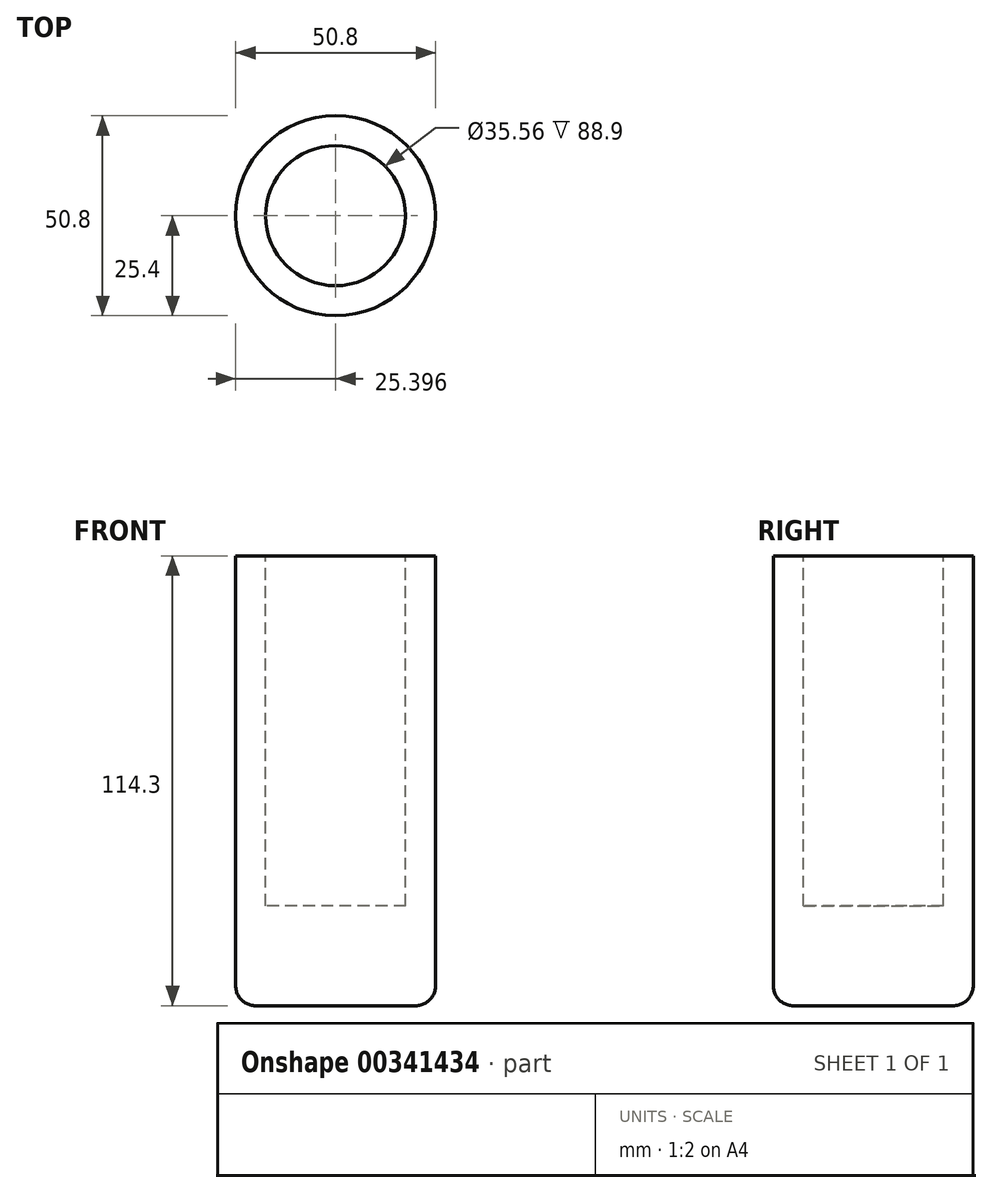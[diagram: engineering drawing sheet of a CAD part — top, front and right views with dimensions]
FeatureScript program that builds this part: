
annotation { "Feature Type Name" : "Feature", "Feature Type Description" : "" }
export const myFeature = defineFeature(function(context is Context, id is Id, definition is map)
    precondition{}
    {
        {
            var Q0;
            Q0=qCreatedBy(makeId("Top.planeOp"),FACE);
            var sketch = newSketch(context, id + "F0", { "sketchPlane" : qUnion([Q0])});
            skCircle(sketch, "E0", {"center": v(4, 0) * mm, "radius": 25.4 * mm});
            skSolve(sketch);
        }
        {
            var Q0;
            Q0 = qSketchRegion(id + "F0", true);
            extrude(context, id + "F1", {"entities" : qUnion([Q0]), "depth" : 76.2 * mm});
        }
        {
            var Q0;
            Q0=makeQuery(id+"F1.opExtrude","CAP_EDGE",EDGE,{"disambiguationData":[OSD([sQuery(id+"F0.wireOp",EDGE,"E0")])],"isStart":true});
            fillet(context, id + "F2", {"entities" : qUnion([Q0]), "radius" : 5.08 * mm, "tangentPropagation" : true, "allowEdgeOverflow" : false});
        }
        {
            var Q0;
            Q0=makeQuery(id+"F1.opExtrude","CAP_FACE",FACE,{"disambiguationData":[OSD([sQuery(id+"F0.wireOp",EDGE,"E0")])],"isStart":false});
            var sketch = newSketch(context, id + "F3", { "sketchPlane" : qUnion([Q0])});
            skCircle(sketch, "E1", {"center": v(4, 0) * mm, "radius": 17.78 * mm});
            skSolve(sketch);
        }
        {
            var Q0;
            Q0=makeQuery(id+"F3.imprint","IMPRINT",FACE,{"disambiguationData":[TD([[makeQuery(id+"F3.imprint","IMPRINT",EDGE,{"derivedFrom":sQuery(id+"F3.wireOp",EDGE,"E1")}),1.0]])]});
            extrude(context, id + "F4", {"entities" : qUnion([Q0]), "operationType" : NewBodyOperationType.REMOVE, "oppositeDirection" : true, "depth" : 50.8 * mm});
        }
        {
            var Q0;
            Q0=makeQuery(id+"F1.opExtrude","CAP_FACE",FACE,{"disambiguationData":[OSD([sQuery(id+"F0.wireOp",EDGE,"E0")])],"isStart":false});
            extrude(context, id + "F5", {"entities" : qUnion([Q0]), "operationType" : NewBodyOperationType.ADD, "depth" : 38.1 * mm});
        }
    });
